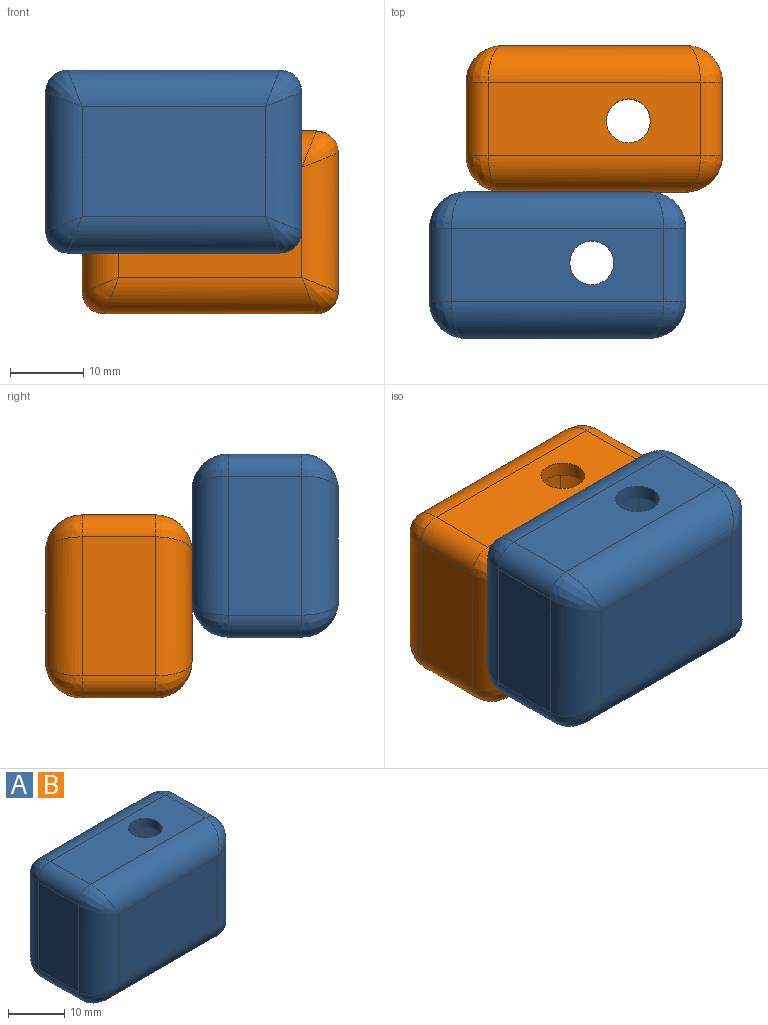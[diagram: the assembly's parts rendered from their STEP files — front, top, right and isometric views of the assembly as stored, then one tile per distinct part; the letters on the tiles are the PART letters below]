
ASSEMBLY  parts=2 mates=1
PART A: 54 faces, bbox 35x20x25 mm
  f0: plane 25x15mm, normal (0,-1,0), area 375mm2, adj f6,f7,f8,f9
  f1: plane 19x10mm, normal (1,0,0), area 190mm2, adj f9,f13,f21,f24
  f2: plane 25x15mm, normal (0,1,0), area 375mm2, adj f10,f11,f12,f13
  f3: plane 19x10mm, normal (-1,0,0), area 190mm2, adj f6,f10,f15,f18
  f4: plane 29x10mm, normal (0,0,-1), area 261.7mm2, adj f7,f11,f15,f21,f27
  f5: plane 29x10mm, normal (0,0,1), area 261.7mm2, adj f8,f12,f18,f24,f26
  f6: cylinder r=3mm len=19mm, axis (0,0,-1), area 82.7mm2, adj f0,f3,f16,f19
  f7: cylinder r=3mm len=29mm, axis (1,0,0), area 129.8mm2, adj f0,f4,f16,f22
  f8: cylinder r=3mm len=29mm, axis (-1,0,0), area 129.8mm2, adj f0,f5,f19,f25
  f9: cylinder r=3mm len=19mm, axis (0,0,1), area 82.7mm2, adj f0,f1,f22,f25
  f10: cylinder r=3mm len=19mm, axis (0,0,1), area 82.7mm2, adj f2,f3,f14,f17
  f11: cylinder r=3mm len=29mm, axis (-1,0,0), area 129.8mm2, adj f2,f4,f14,f20
  f12: cylinder r=3mm len=29mm, axis (1,0,0), area 129.8mm2, adj f2,f5,f17,f23
  f13: cylinder r=3mm len=19mm, axis (0,0,-1), area 82.7mm2, adj f1,f2,f20,f23
  f14: bspline ~3.13x3mm, area 5mm2, adj f10,f11,f15
  f15: cylinder r=1mm len=10mm, axis (0,-1,0), area 15.7mm2, adj f3,f4,f14,f16
  f16: bspline ~3.52x3mm, area 5mm2, adj f6,f7,f15
  f17: bspline ~3.52x3mm, area 5mm2, adj f10,f12,f18
  f18: cylinder r=1mm len=10mm, axis (0,1,0), area 15.7mm2, adj f3,f5,f17,f19
  f19: bspline ~3.13x3mm, area 5mm2, adj f6,f8,f18
  f20: bspline ~3.13x3mm, area 5mm2, adj f11,f13,f21
  f21: cylinder r=1mm len=10mm, axis (0,1,0), area 15.7mm2, adj f1,f4,f20,f22
  f22: bspline ~3.52x3mm, area 5mm2, adj f7,f9,f21
  f23: bspline ~3.52x3mm, area 5mm2, adj f12,f13,f24
  f24: cylinder r=1mm len=10mm, axis (0,-1,0), area 15.7mm2, adj f1,f5,f23,f25
  f25: bspline ~3.13x3mm, area 5mm2, adj f8,f9,f24
  f26: cylinder r=3mm len=6mm, axis (0,0,-1), area 37.7mm2, adj f5,f48
  f27: cylinder r=3mm len=6mm, axis (0,0,-1), area 37.7mm2, adj f4,f49
  f28: bspline ~5.26x5mm, area 24.5mm2, adj f29,f44,f45
  f29: cylinder r=3mm len=10mm, axis (0,-1,0), area 47.1mm2, adj f28,f30,f48,f52
  f30: bspline ~6.03x5mm, area 24.5mm2, adj f29,f40,f41
  f31: bspline ~6.03x5mm, area 24.5mm2, adj f32,f44,f46
  f32: cylinder r=3mm len=10mm, axis (0,1,0), area 47.1mm2, adj f31,f33,f49,f52
  f33: bspline ~5.26x5mm, area 24.5mm2, adj f32,f40,f42
  f34: bspline ~5.26x5mm, area 24.5mm2, adj f35,f45,f47
  f35: cylinder r=3mm len=10mm, axis (0,1,0), area 47.1mm2, adj f34,f36,f48,f50
  f36: bspline ~6.03x5mm, area 24.5mm2, adj f35,f41,f43
  f37: bspline ~6.03x5mm, area 24.5mm2, adj f38,f46,f47
  f38: cylinder r=3mm len=10mm, axis (0,-1,0), area 47.1mm2, adj f37,f39,f49,f50
  f39: bspline ~5.26x5mm, area 24.5mm2, adj f38,f42,f43
  f40: cylinder r=5mm len=19mm, axis (0,0,-1), area 137.8mm2, adj f30,f33,f51,f52
  f41: cylinder r=5mm len=29mm, axis (1,0,0), area 216.3mm2, adj f30,f36,f48,f51
  f42: cylinder r=5mm len=29mm, axis (-1,0,0), area 216.3mm2, adj f33,f39,f49,f51
  f43: cylinder r=5mm len=19mm, axis (0,0,1), area 137.8mm2, adj f36,f39,f50,f51
  f44: cylinder r=5mm len=19mm, axis (0,0,1), area 137.8mm2, adj f28,f31,f52,f53
  f45: cylinder r=5mm len=29mm, axis (-1,0,0), area 216.3mm2, adj f28,f34,f48,f53
  f46: cylinder r=5mm len=29mm, axis (1,0,0), area 216.3mm2, adj f31,f37,f49,f53
  f47: cylinder r=5mm len=19mm, axis (0,0,-1), area 137.8mm2, adj f34,f37,f50,f53
  f48: plane 29x10mm, normal (0,0,-1), area 261.7mm2, adj f26,f29,f35,f41,f45
  f49: plane 29x10mm, normal (0,0,1), area 261.7mm2, adj f27,f32,f38,f42,f46
  f50: plane 19x10mm, normal (1,0,0), area 190mm2, adj f35,f38,f43,f47
  f51: plane 25x15mm, normal (0,-1,0), area 375mm2, adj f40,f41,f42,f43
  f52: plane 19x10mm, normal (-1,0,0), area 190mm2, adj f29,f32,f40,f44
  f53: plane 25x15mm, normal (0,1,0), area 375mm2, adj f44,f45,f46,f47
PART B: same geometry as A
PLACE A t=(-12.9,-15.93,8.38)mm fixed
PLACE B rot(axis=(1,0,0),180deg) t=(-7.9,24.07,25.06)mm
MATE planar B.f53 <-> A.f53  axis (0,-1,0) through (-25.4,4.07,12.56)mm
